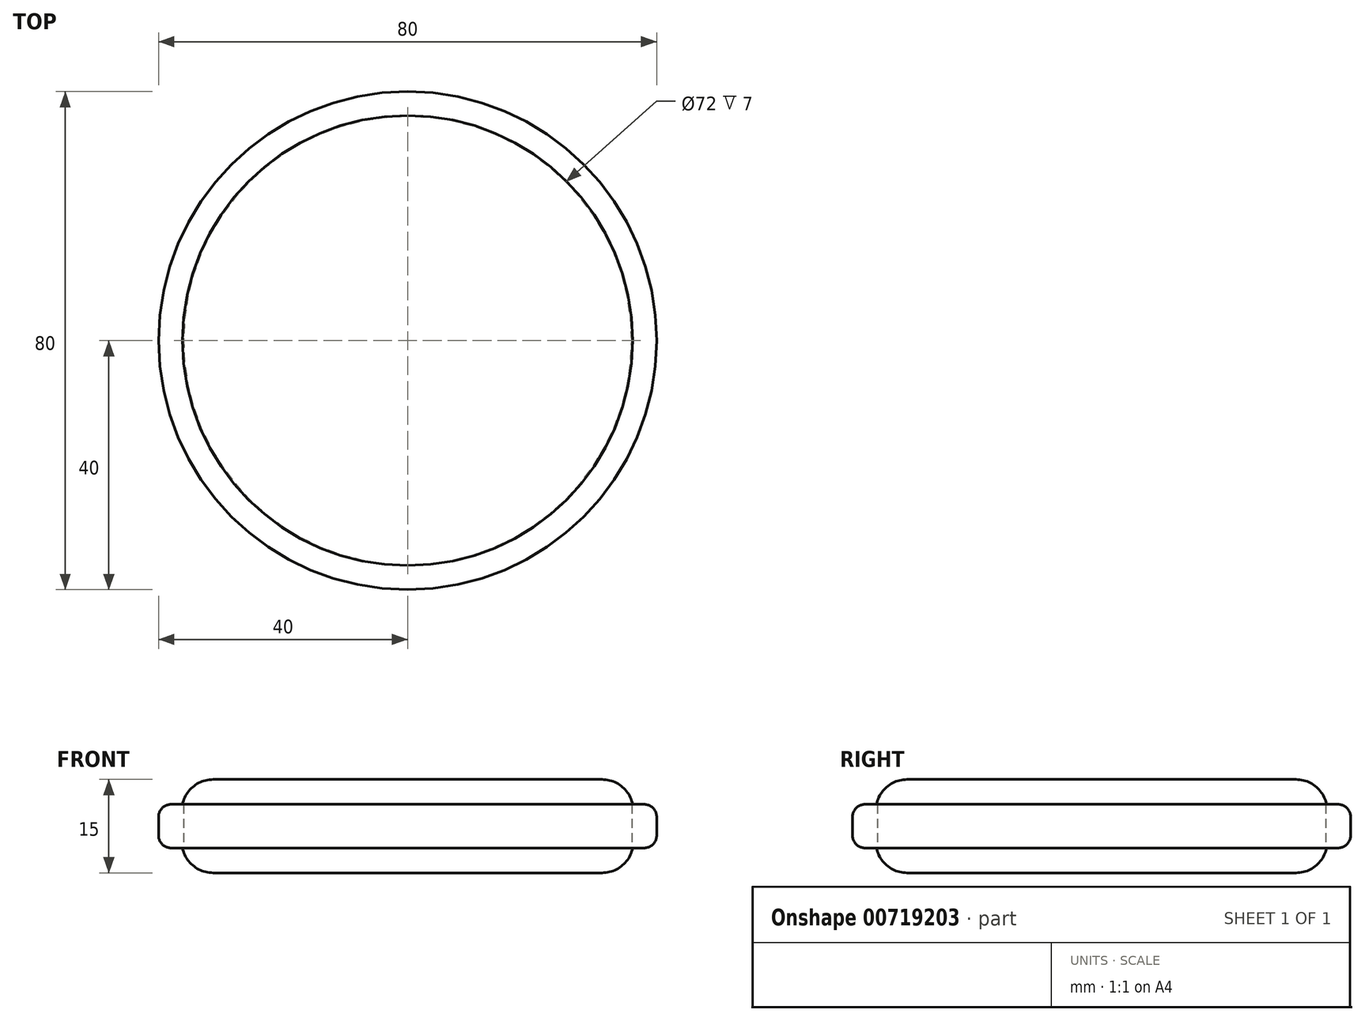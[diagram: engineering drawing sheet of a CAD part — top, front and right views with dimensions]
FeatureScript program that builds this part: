
annotation { "Feature Type Name" : "Feature", "Feature Type Description" : "" }
export const myFeature = defineFeature(function(context is Context, id is Id, definition is map)
    precondition{}
    {
        {
            assignVariable(context, id + "F0", {"name" : "depth", "anyValue" : 7 * mm});
        }
        {
            assignVariable(context, id + "F1", {"name" : "height", "anyValue" : 15 * mm});
        }
        {
            var Q0;
            Q0=qCreatedBy(makeId("Top.planeOp"),FACE);
            var sketch = newSketch(context, id + "F2", { "sketchPlane" : qUnion([Q0])});
            skCircle(sketch, "E0", {"center": v(0, 0) * mm, "radius": 40 * mm});
            skCircle(sketch, "E1", {"center": v(0, 0) * mm, "radius": 36 * mm});
            skSolve(sketch);
        }
        {
            var Q0;
            Q0=makeQuery(id+"F2.imprint","IMPRINT",FACE,{"disambiguationData":[TD([[makeQuery(id+"F2.imprint","IMPRINT",EDGE,{"derivedFrom":sQuery(id+"F2.wireOp",EDGE,"E0")}),1.0]])]});
            extrude(context, id + "F3", {"entities" : qUnion([Q0]), "endBound" : BoundingType.SYMMETRIC, "depth" : getVariable(context, 'depth'), "offsetDistance" : 25 * mm});
        }
        {
            var Q0;
            Q0=qCreatedBy(makeId("Top.planeOp"),FACE);
            var sketch = newSketch(context, id + "F4", { "sketchPlane" : qUnion([Q0])});
            skCircle(sketch, "E2", {"center": v(0, 0) * mm, "radius": 36.25 * mm});
            skSolve(sketch);
        }
        {
            var Q0;
            Q0 = qSketchRegion(id + "F4", true);
            extrude(context, id + "F5", {"entities" : qUnion([Q0]), "endBound" : BoundingType.SYMMETRIC, "depth" : getVariable(context, 'height'), "offsetDistance" : 25 * mm});
        }
        {
            var Q0;
            Q0=makeQuery(id+"F5.opExtrude","CAP_FACE",FACE,{"disambiguationData":[OSD([sQuery(id+"F4.wireOp",EDGE,"E2")])],"isStart":false});
            var Q1;
            Q1=makeQuery(id+"F5.opExtrude","CAP_FACE",FACE,{"disambiguationData":[OSD([sQuery(id+"F4.wireOp",EDGE,"E2")])],"isStart":true});
            fillet(context, id + "F6", {"entities" : qUnion([Q0, Q1]), "radius" : 5 * mm, "tangentPropagation" : true, "allowEdgeOverflow" : false});
        }
        {
            var Q0;
            Q0=makeQuery(id+"F3.opExtrude","SWEPT_BODY",BODY,{"disambiguationData":[OSD([sQuery(id+"F2.wireOp",EDGE,"E0"),sQuery(id+"F2.wireOp",EDGE,"E1")])]});
            transform(context, id + "F7", {"entities" : qUnion([Q0]), "transformType" : TransformType.TRANSLATION_3D, "dx" : 0 * mm, "dy" : 0 * mm, "dz" : 0 * mm, "makeCopy" : true});
        }
        {
            var Q0;
            Q0=makeQuery(id+"F7.opPattern","COPY",BODY,{"derivedFrom":makeQuery(id+"F3.opExtrude","SWEPT_BODY",BODY,{"disambiguationData":[OSD([sQuery(id+"F2.wireOp",EDGE,"E0"),sQuery(id+"F2.wireOp",EDGE,"E1")])]}),"instanceName":"1"});
            var Q1;
            Q1=makeQuery(id+"F5.opExtrude","SWEPT_BODY",BODY,{"disambiguationData":[OSD([sQuery(id+"F4.wireOp",EDGE,"E2")])]});
            booleanBodies(context, id + "F8", {"operationType" : BooleanOperationType.SUBTRACTION, "tools" : qUnion([Q0]), "targets" : qUnion([Q1])});
        }
        {
            var Q0;
            Q0=makeQuery(id+"F3.opExtrude","SWEPT_FACE",FACE,{"disambiguationData":[OSD([sQuery(id+"F2.wireOp",EDGE,"E0")])]});
            fillet(context, id + "F9", {"entities" : qUnion([Q0]), "radius" : 2 * mm, "tangentPropagation" : true, "allowEdgeOverflow" : false});
        }
    });
